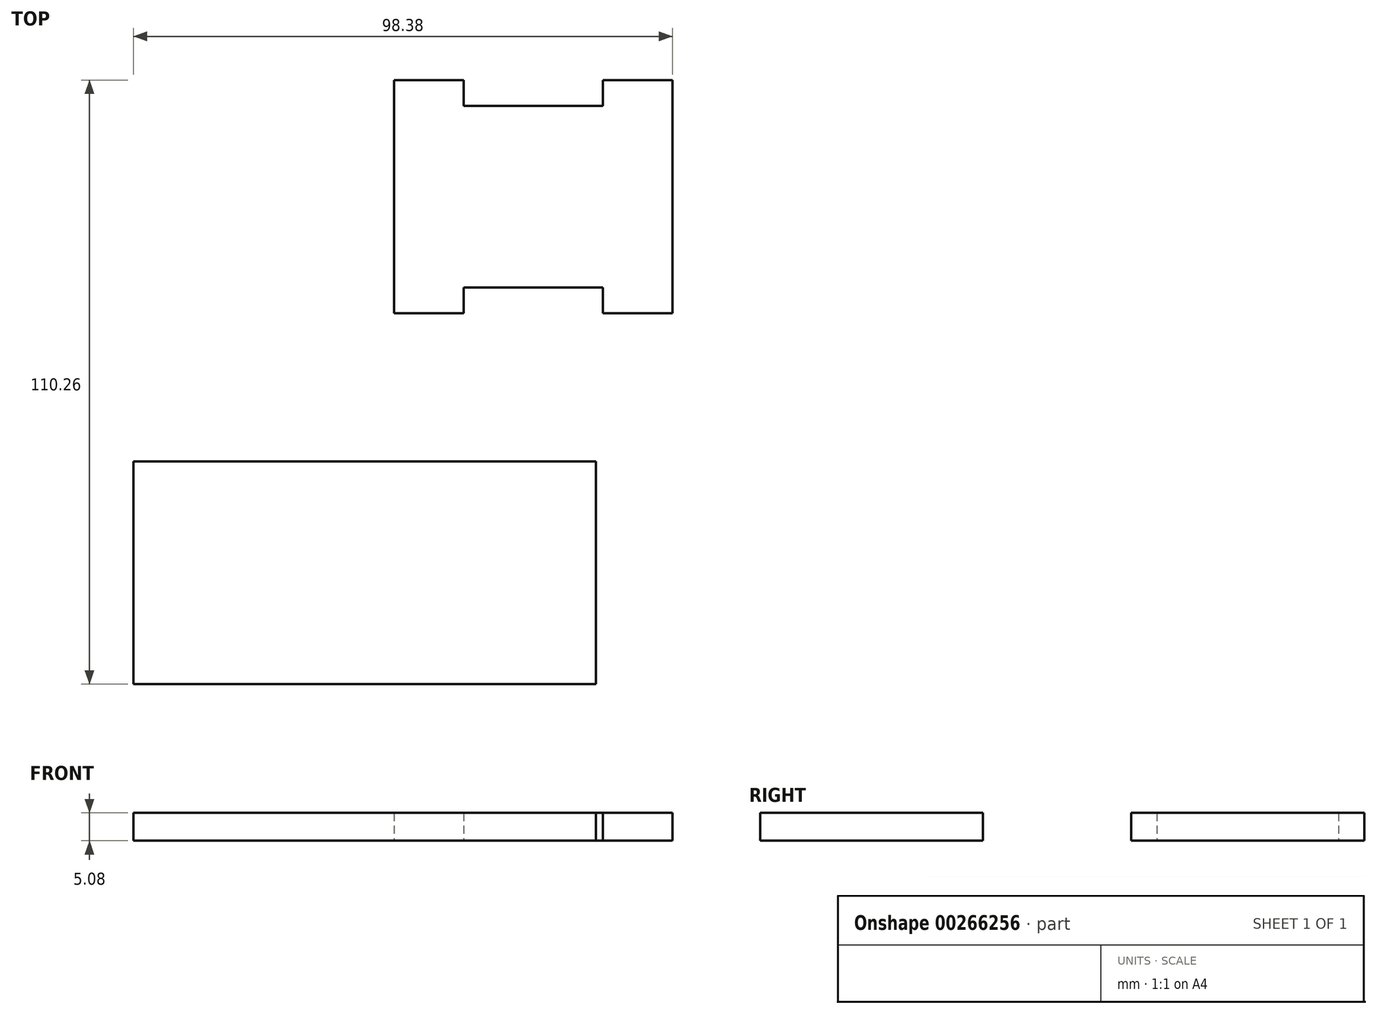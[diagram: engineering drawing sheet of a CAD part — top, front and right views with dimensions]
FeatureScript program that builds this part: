
annotation { "Feature Type Name" : "Feature", "Feature Type Description" : "" }
export const myFeature = defineFeature(function(context is Context, id is Id, definition is map)
    precondition{}
    {
        {
            var Q0;
            Q0=qCreatedBy(makeId("Top.planeOp"),FACE);
            var sketch = newSketch(context, id + "F0", { "sketchPlane" : qUnion([Q0])});
            skLineSegment(sketch, "E0.right", {"start": v(52.95, 0) * mm, "end": v(52.95, -40.64) * mm});
            skLineSegment(sketch, "E1.top", {"start": v(-31.45, -40.64) * mm, "end": v(14.27, -40.64) * mm});
            skLineSegment(sketch, "E1.left", {"start": v(-31.45, -40.64) * mm, "end": v(-31.45, -40.64) * mm});
            skLineSegment(sketch, "E1.right", {"start": v(14.27, -40.64) * mm, "end": v(14.27, -40.64) * mm});
            skLineSegment(sketch, "E2.MirrorCS", {"start": v(-31.44, 0) * mm, "end": v(14.27, 0) * mm});
            skLineSegment(sketch, "E3.MirrorCS", {"start": v(-31.44, 0) * mm, "end": v(-31.44, 0) * mm});
            skLineSegment(sketch, "E4.MirrorCS", {"start": v(14.27, 0) * mm, "end": v(14.27, 0) * mm});
            skLineSegment(sketch, "E5.trimOffspring", {"start": v(14.27, 0) * mm, "end": v(52.95, 0) * mm});
            skLineSegment(sketch, "E6.trimOffspring", {"start": v(14.27, -40.64) * mm, "end": v(52.95, -40.64) * mm});
            skPoint(sketch, "E7.visualSharp", {"position": v(-34.45, -7.49) * mm});
            skPoint(sketch, "E8.visualSharp", {"position": v(-34.45, -33.02) * mm});
            skLineSegment(sketch, "E9", {"start": v(-31.44, 0) * mm, "end": v(-31.45, -40.64) * mm});
            skPoint(sketch, "E10.right.end.orphan", {"position": v(-59.38, 0) * mm});
            skPoint(sketch, "E0.top.start.orphan", {"position": v(-59.4, -40.64) * mm});
            skSolve(sketch);
        }
        {
            var Q0;
            Q0=qCreatedBy(makeId("Top.planeOp"),FACE);
            var sketch = newSketch(context, id + "F1", { "sketchPlane" : qUnion([Q0])});
            skLineSegment(sketch, "E11.bottom", {"start": v(16.13, 69.62) * mm, "end": v(28.83, 69.62) * mm});
            skLineSegment(sketch, "E11.top", {"start": v(16.13, 27.04) * mm, "end": v(28.83, 27.04) * mm});
            skLineSegment(sketch, "E11.left", {"start": v(16.13, 69.62) * mm, "end": v(16.13, 27.04) * mm});
            skLineSegment(sketch, "E11.right", {"start": v(66.93, 69.62) * mm, "end": v(66.93, 27.04) * mm});
            skLineSegment(sketch, "E12.top", {"start": v(41.53, 31.74) * mm, "end": v(28.83, 31.74) * mm});
            skLineSegment(sketch, "E12.right", {"start": v(28.83, 27.04) * mm, "end": v(28.83, 31.74) * mm});
            skLineSegment(sketch, "E13.top", {"start": v(41.53, 31.74) * mm, "end": v(54.23, 31.74) * mm});
            skLineSegment(sketch, "E13.right", {"start": v(54.23, 27.04) * mm, "end": v(54.23, 31.74) * mm});
            skLineSegment(sketch, "E14.MirrorCS", {"start": v(41.53, 64.92) * mm, "end": v(28.83, 64.92) * mm});
            skLineSegment(sketch, "E15.MirrorCS", {"start": v(28.83, 69.62) * mm, "end": v(28.83, 64.92) * mm});
            skLineSegment(sketch, "E16.MirrorCS", {"start": v(41.53, 64.92) * mm, "end": v(54.23, 64.92) * mm});
            skLineSegment(sketch, "E17.MirrorCS", {"start": v(54.23, 69.62) * mm, "end": v(54.23, 64.92) * mm});
            skLineSegment(sketch, "E18.trimOffspring", {"start": v(54.23, 69.62) * mm, "end": v(66.93, 69.62) * mm});
            skLineSegment(sketch, "E19.trimOffspring", {"start": v(54.23, 27.04) * mm, "end": v(66.93, 27.04) * mm});
            skSolve(sketch);
        }
        {
            var Q0;
            Q0=makeQuery(id+"F1.imprint","IMPRINT",FACE,{"disambiguationData":[TD([[makeQuery(id+"F1.imprint","IMPRINT",EDGE,{"derivedFrom":sQuery(id+"F1.wireOp",EDGE,"E11.bottom")}),-1.0]])]});
            extrude(context, id + "F2", {"entities" : qUnion([Q0]), "depth" : 5.08 * mm});
        }
        {
            var Q0;
            Q0 = qSketchRegion(id + "F0", true);
            extrude(context, id + "F3", {"entities" : qUnion([Q0]), "depth" : 5.08 * mm});
        }
    });
